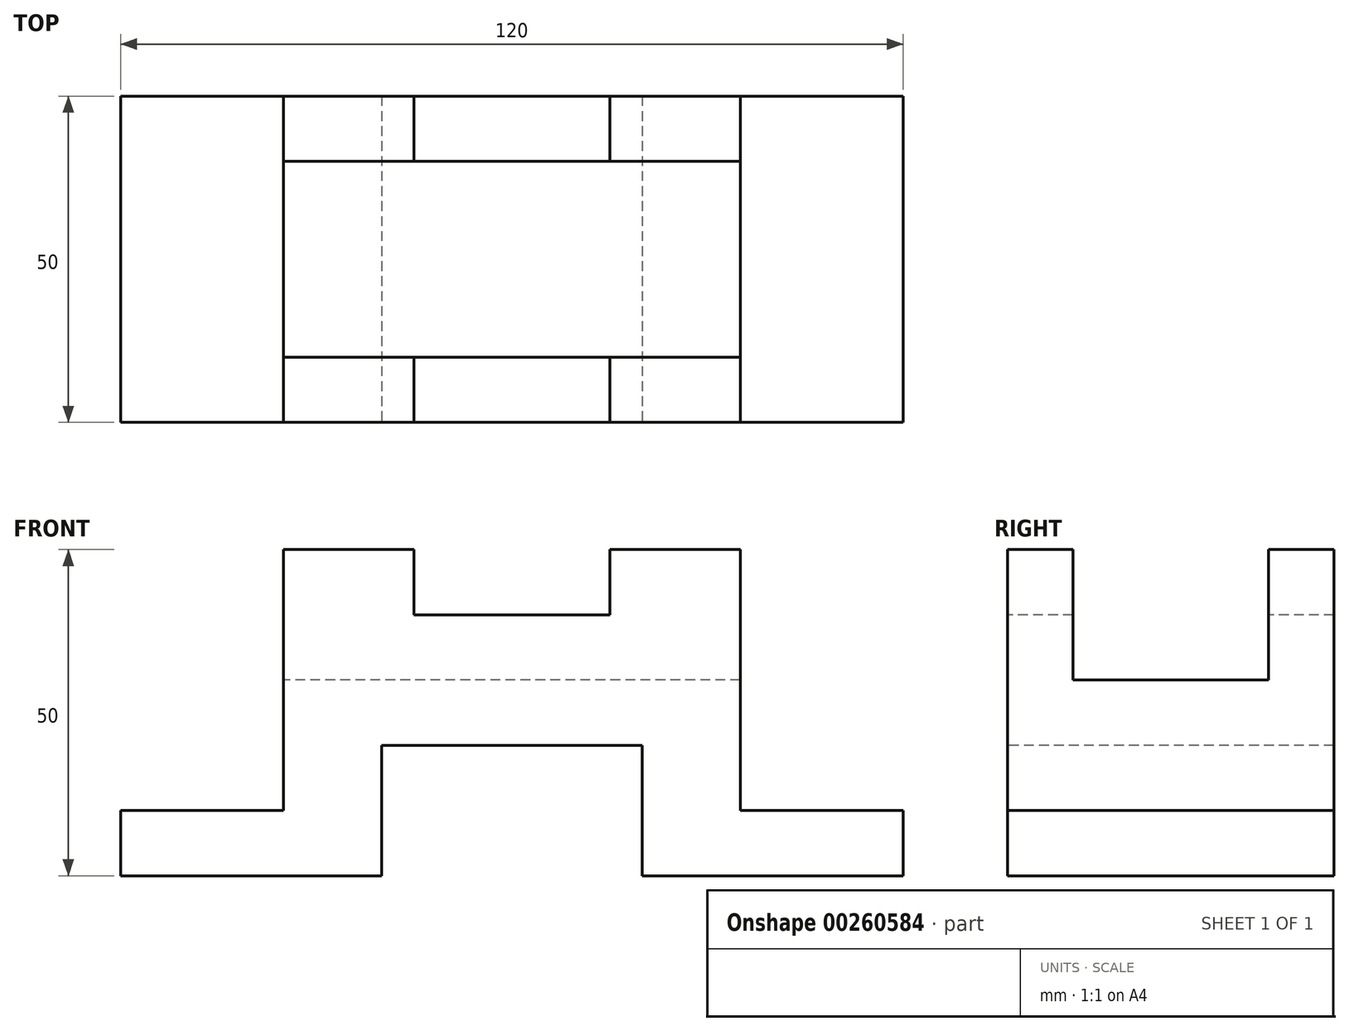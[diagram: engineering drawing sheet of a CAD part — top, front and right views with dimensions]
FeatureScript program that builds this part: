
annotation { "Feature Type Name" : "Feature", "Feature Type Description" : "" }
export const myFeature = defineFeature(function(context is Context, id is Id, definition is map)
    precondition{}
    {
        {
            assignVariable(context, id + "F0", {"name" : "A", "anyValue" : 50});
        }
        {
            assignVariable(context, id + "F1", {"name" : "B", "anyValue" : 50});
        }
        {
            assignVariable(context, id + "F2", {"name" : "C", "anyValue" : 120});
        }
        {
            var Q0;
            Q0=qCreatedBy(makeId("Top.planeOp"),FACE);
            var sketch = newSketch(context, id + "F3", { "sketchPlane" : qUnion([Q0])});
            skLineSegment(sketch, "E0.bottom", {"start": v(60, -25) * mm, "end": v(-60, -25) * mm});
            skLineSegment(sketch, "E0.top", {"start": v(60, 25) * mm, "end": v(-60, 25) * mm});
            skLineSegment(sketch, "E0.left", {"start": v(60, -25) * mm, "end": v(60, 25) * mm});
            skLineSegment(sketch, "E0.right", {"start": v(-60, -25) * mm, "end": v(-60, 25) * mm});
            skPoint(sketch, "E0.middle", {"position": v(0, 0) * mm});
            skSolve(sketch);
        }
        {
            var Q0;
            Q0 = qSketchRegion(id + "F3", true);
            extrude(context, id + "F4", {"entities" : qUnion([Q0]), "depth" : (getVariable(context, 'B')) * mm});
        }
        {
            var Q0;
            Q0=makeQuery(id+"F4.opExtrude","SWEPT_FACE",FACE,{"disambiguationData":[OSD([sQuery(id+"F3.wireOp",EDGE,"E0.bottom")])]});
            var sketch = newSketch(context, id + "F5", { "sketchPlane" : qUnion([Q0])});
            skLineSegment(sketch, "E1.bottom", {"start": v(60, 50) * mm, "end": v(35, 50) * mm});
            skLineSegment(sketch, "E1.top", {"start": v(60, 10) * mm, "end": v(35, 10) * mm});
            skLineSegment(sketch, "E1.left", {"start": v(60, 50) * mm, "end": v(60, 10) * mm});
            skLineSegment(sketch, "E1.right", {"start": v(35, 50) * mm, "end": v(35, 10) * mm});
            skSolve(sketch);
        }
        {
            var Q0;
            Q0 = qSketchRegion(id + "F5", true);
            extrude(context, id + "F6", {"entities" : qUnion([Q0]), "operationType" : NewBodyOperationType.REMOVE, "oppositeDirection" : true, "depth" : (getVariable(context, 'A')) * mm});
        }
        {
            var Q0;
            Q0=makeQuery(id+"F4.opExtrude","SWEPT_FACE",FACE,{"disambiguationData":[OSD([sQuery(id+"F3.wireOp",EDGE,"E0.bottom")])]});
            var sketch = newSketch(context, id + "F7", { "sketchPlane" : qUnion([Q0])});
            skLineSegment(sketch, "E2.bottom", {"start": v(-60, 50) * mm, "end": v(-35, 50) * mm});
            skLineSegment(sketch, "E2.top", {"start": v(-60, 10) * mm, "end": v(-35, 10) * mm});
            skLineSegment(sketch, "E2.left", {"start": v(-60, 50) * mm, "end": v(-60, 10) * mm});
            skLineSegment(sketch, "E2.right", {"start": v(-35, 50) * mm, "end": v(-35, 10) * mm});
            skSolve(sketch);
        }
        {
            var Q0;
            Q0 = qSketchRegion(id + "F7", true);
            extrude(context, id + "F8", {"entities" : qUnion([Q0]), "operationType" : NewBodyOperationType.REMOVE, "oppositeDirection" : true, "depth" : (getVariable(context, 'A')) * mm});
        }
        {
            var Q0;
            Q0=makeQuery(id+"F4.opExtrude","SWEPT_FACE",FACE,{"disambiguationData":[OSD([sQuery(id+"F3.wireOp",EDGE,"E0.bottom")])]});
            var sketch = newSketch(context, id + "F9", { "sketchPlane" : qUnion([Q0])});
            skLineSegment(sketch, "E3.bottom", {"start": v(-20, 0) * mm, "end": v(20, 0) * mm});
            skLineSegment(sketch, "E3.top", {"start": v(-20, 20) * mm, "end": v(20, 20) * mm});
            skLineSegment(sketch, "E3.left", {"start": v(-20, 0) * mm, "end": v(-20, 20) * mm});
            skLineSegment(sketch, "E3.right", {"start": v(20, 0) * mm, "end": v(20, 20) * mm});
            skPoint(sketch, "E3.middle", {"position": v(0, 10) * mm});
            skSolve(sketch);
        }
        {
            var Q0;
            Q0 = qSketchRegion(id + "F9", true);
            extrude(context, id + "F10", {"entities" : qUnion([Q0]), "operationType" : NewBodyOperationType.REMOVE, "oppositeDirection" : true, "depth" : (getVariable(context, 'A')) * mm});
        }
        {
            var Q0;
            Q0=makeQuery(id+"F4.opExtrude","SWEPT_FACE",FACE,{"disambiguationData":[OSD([sQuery(id+"F3.wireOp",EDGE,"E0.bottom")])]});
            var sketch = newSketch(context, id + "F11", { "sketchPlane" : qUnion([Q0])});
            skLineSegment(sketch, "E4.bottom", {"start": v(-15, 50) * mm, "end": v(15, 50) * mm});
            skLineSegment(sketch, "E4.top", {"start": v(-15, 40) * mm, "end": v(15, 40) * mm});
            skLineSegment(sketch, "E4.left", {"start": v(-15, 50) * mm, "end": v(-15, 40) * mm});
            skLineSegment(sketch, "E4.right", {"start": v(15, 50) * mm, "end": v(15, 40) * mm});
            skPoint(sketch, "E4.middle", {"position": v(0, 45) * mm});
            skSolve(sketch);
        }
        {
            var Q0;
            Q0 = qSketchRegion(id + "F11", true);
            extrude(context, id + "F12", {"entities" : qUnion([Q0]), "operationType" : NewBodyOperationType.REMOVE, "oppositeDirection" : true, "depth" : (getVariable(context, 'A')) * mm});
        }
        {
            var Q0;
            Q0=makeQuery(id+"F8.boolean.opBoolean","COPY",FACE,{"derivedFrom":makeQuery(id+"F8.opExtrude","SWEPT_FACE",FACE,{"disambiguationData":[OSD([sQuery(id+"F7.wireOp",EDGE,"E2.right")])]})});
            var sketch = newSketch(context, id + "F13", { "sketchPlane" : qUnion([Q0])});
            skLineSegment(sketch, "E5.bottom", {"start": v(-15, 50) * mm, "end": v(15, 50) * mm});
            skLineSegment(sketch, "E5.top", {"start": v(-15, 30) * mm, "end": v(15, 30) * mm});
            skLineSegment(sketch, "E5.left", {"start": v(-15, 50) * mm, "end": v(-15, 30) * mm});
            skLineSegment(sketch, "E5.right", {"start": v(15, 50) * mm, "end": v(15, 30) * mm});
            skPoint(sketch, "E5.middle", {"position": v(0, 40) * mm});
            skSolve(sketch);
        }
        {
            var Q0;
            Q0 = qSketchRegion(id + "F13", true);
            extrude(context, id + "F14", {"entities" : qUnion([Q0]), "operationType" : NewBodyOperationType.REMOVE, "oppositeDirection" : true, "depth" : (getVariable(context, 'C')) * mm});
        }
    });
